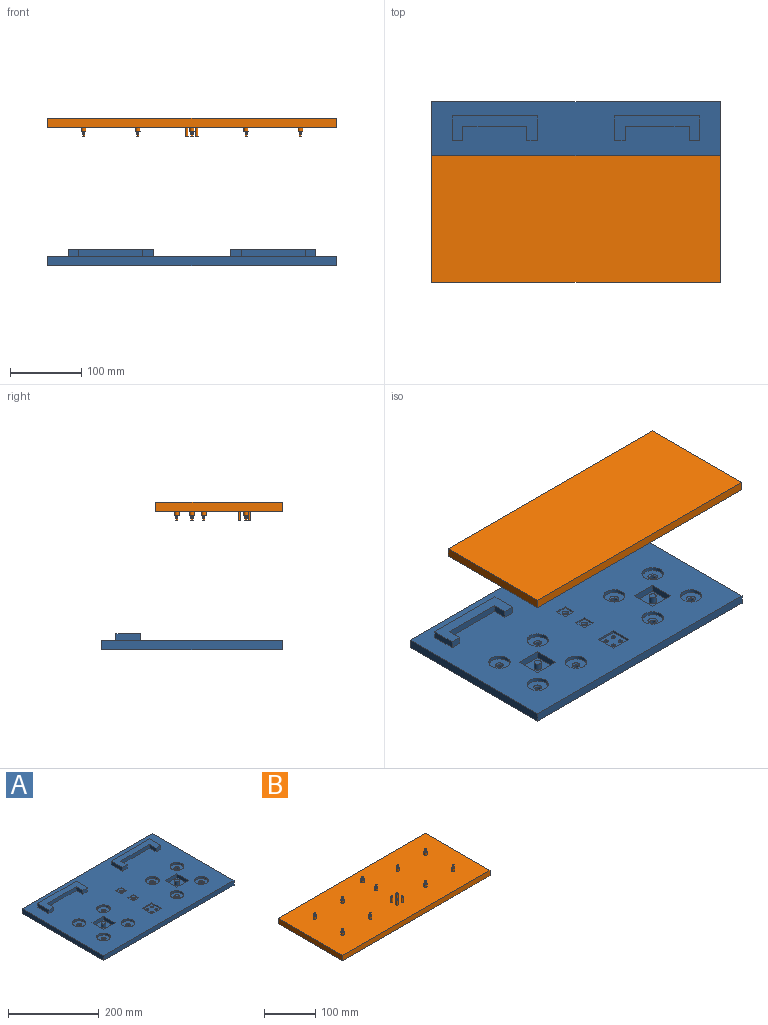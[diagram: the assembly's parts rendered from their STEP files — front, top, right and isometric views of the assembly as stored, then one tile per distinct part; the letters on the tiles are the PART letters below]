
ASSEMBLY  parts=2 mates=2
PART A: 93 faces, bbox 406.4x254x22.7 mm
  f0: plane 406.4x254mm, normal (0,0,1), area 88690.8mm2, adj f2,f3,f4,f5,f6,f7,f8,f9
  f1: plane 406.4x254mm, normal (0,0,-1), area 102653.3mm2, adj f2,f3,f4,f5,f21,f22,f23,f24
  f2: plane 406.4x12.7mm, normal (0,1,0), area 5161.3mm2, adj f0,f1,f3,f5
  f3: plane 254x12.7mm, normal (-1,0,0), area 3225.8mm2, adj f0,f1,f2,f4
  f4: plane 406.4x12.7mm, normal (0,-1,0), area 5161.3mm2, adj f0,f1,f3,f5
  f5: plane 254x12.7mm, normal (1,0,0), area 3225.8mm2, adj f0,f1,f2,f4
  f6: plane 17.15x2mm, normal (0,-1,0), area 34.3mm2, adj f0,f7,f9,f10
  f7: plane 17.15x2mm, normal (1,0,0), area 34.3mm2, adj f0,f6,f8,f10
  f8: plane 17.15x2mm, normal (0,1,0), area 34.3mm2, adj f0,f7,f9,f10
  f9: plane 17.15x2mm, normal (-1,0,0), area 34.3mm2, adj f0,f6,f8,f10
  f10: plane 17.15x17.15mm, normal (0,0,1), area 226.3mm2, adj f6,f7,f8,f9,f83
  f11: plane 17.15x2mm, normal (-1,0,0), area 34.3mm2, adj f0,f12,f14,f15
  f12: plane 17.15x2mm, normal (0,-1,0), area 34.3mm2, adj f0,f11,f13,f15
  f13: plane 17.15x2mm, normal (1,0,0), area 34.3mm2, adj f0,f12,f14,f15
  f14: plane 17.15x2mm, normal (0,1,0), area 34.3mm2, adj f0,f11,f13,f15
  f15: plane 17.15x17.15mm, normal (0,0,1), area 226.3mm2, adj f11,f12,f13,f14,f84
  f16: plane 30x3mm, normal (0,-1,0), area 90mm2, adj f0,f17,f19,f20
  f17: plane 30x3mm, normal (1,0,0), area 90mm2, adj f0,f16,f18,f20
  f18: plane 30x3mm, normal (0,1,0), area 90mm2, adj f0,f17,f19,f20
  f19: plane 30x3mm, normal (-1,0,0), area 90mm2, adj f0,f16,f18,f20
  f20: plane 30x30mm, normal (0,0,1), area 786.9mm2, adj f16,f17,f18,f19,f21,f22,f23,f24
  f21: cylinder r=3mm len=9.7mm, axis (0,0,1), area 182.8mm2, adj f1,f20
  f22: cylinder r=3mm len=9.7mm, axis (0,0,1), area 182.8mm2, adj f1,f20
  f23: cylinder r=3mm len=9.7mm, axis (0,0,1), area 182.8mm2, adj f1,f20
  f24: cylinder r=3mm len=9.7mm, axis (0,0,1), area 182.8mm2, adj f1,f20
  f25: cylinder r=15mm len=30mm, axis (0,0,1), area 471.2mm2, adj f0,f26
  f26: plane 30x30mm, normal (0,0,1), area 614.1mm2, adj f25,f92
  f27: cylinder r=15mm len=30mm, axis (0,0,1), area 471.2mm2, adj f0,f28
  f28: plane 30x30mm, normal (0,0,1), area 573.8mm2, adj f27,f85
  f29: cylinder r=15mm len=30mm, axis (0,0,1), area 471.2mm2, adj f0,f30
  f30: plane 30x30mm, normal (0,0,1), area 573.8mm2, adj f29,f86
  f31: cylinder r=15mm len=30mm, axis (0,0,1), area 471.2mm2, adj f0,f32
  f32: plane 30x30mm, normal (0,0,1), area 573.8mm2, adj f31,f87
  f33: cylinder r=15mm len=30mm, axis (0,0,1), area 471.2mm2, adj f0,f34
  f34: plane 30x30mm, normal (0,0,1), area 614.1mm2, adj f33,f89
  f35: cylinder r=15mm len=30mm, axis (0,0,1), area 471.2mm2, adj f0,f36
  f36: plane 30x30mm, normal (0,0,1), area 614.1mm2, adj f35,f90
  f37: cylinder r=15mm len=30mm, axis (0,0,1), area 471.2mm2, adj f0,f38
  f38: plane 30x30mm, normal (0,0,1), area 614.1mm2, adj f37,f91
  f39: cylinder r=15mm len=30mm, axis (0,0,1), area 471.2mm2, adj f0,f40
  f40: plane 30x30mm, normal (0,0,1), area 573.8mm2, adj f39,f88
  f41: cylinder r=3.97mm len=7.94mm, axis (0,0,1), area 128.7mm2, adj f1,f92
  f42: cylinder r=3.97mm len=7.94mm, axis (0,0,1), area 155.4mm2, adj f1,f85
  f43: cylinder r=3.97mm len=7.94mm, axis (0,0,1), area 155.4mm2, adj f1,f86
  f44: cylinder r=3.97mm len=7.94mm, axis (0,0,1), area 155.4mm2, adj f1,f87
  f45: cylinder r=3.97mm len=7.94mm, axis (0,0,1), area 128.7mm2, adj f1,f89
  f46: cylinder r=3.97mm len=7.94mm, axis (0,0,1), area 128.7mm2, adj f1,f90
  f47: cylinder r=3.97mm len=7.94mm, axis (0,0,1), area 128.7mm2, adj f1,f91
  f48: cylinder r=3.97mm len=7.94mm, axis (0,0,1), area 155.4mm2, adj f1,f88
  f49: plane 36x10mm, normal (-1,0,0), area 360mm2, adj f0,f50,f52,f53
  f50: plane 36x10mm, normal (0,-1,0), area 360mm2, adj f0,f49,f51,f53
  f51: plane 36x10mm, normal (1,0,0), area 360mm2, adj f0,f50,f52,f53
  f52: plane 36x10mm, normal (0,1,0), area 360mm2, adj f0,f49,f51,f53
  f53: plane 36x36mm, normal (0,0,1), area 1217.5mm2, adj f49,f50,f51,f52,f61
  f54: plane 36x10mm, normal (0,-1,0), area 360mm2, adj f0,f55,f57,f58
  f55: plane 36x10mm, normal (1,0,0), area 360mm2, adj f0,f54,f56,f58
  f56: plane 36x10mm, normal (0,1,0), area 360mm2, adj f0,f55,f57,f58
  f57: plane 36x10mm, normal (-1,0,0), area 360mm2, adj f0,f54,f56,f58
  f58: plane 36x36mm, normal (0,0,1), area 1217.5mm2, adj f54,f55,f56,f57,f59
  f59: cylinder r=5mm len=10mm, axis (0,0,-1), area 314.2mm2, adj f58,f60
  f60: plane 10x10mm, normal (0,0,1), area 78.5mm2, adj f59
  f61: cylinder r=5mm len=10mm, axis (0,0,-1), area 314.2mm2, adj f53,f62
  f62: plane 10x10mm, normal (0,0,1), area 78.5mm2, adj f61
  f63: plane 35x10mm, normal (-1,0,0), area 350mm2, adj f0,f64,f70,f71
  f64: plane 15x10mm, normal (0,-1,0), area 150mm2, adj f0,f63,f65,f71
  f65: plane 20x10mm, normal (1,0,0), area 200mm2, adj f0,f64,f66,f71
  f66: plane 90x10mm, normal (0,-1,0), area 900mm2, adj f0,f65,f67,f71
  f67: plane 20x10mm, normal (-1,0,0), area 200mm2, adj f0,f66,f68,f71
  f68: plane 15x10mm, normal (0,-1,0), area 150mm2, adj f0,f67,f69,f71
  f69: plane 35x10mm, normal (1,0,0), area 350mm2, adj f0,f68,f70,f71
  f70: plane 120x10mm, normal (0,1,0), area 1200mm2, adj f0,f63,f69,f71
  f71: plane 120x35mm, normal (0,0,1), area 2400mm2, adj f63,f64,f65,f66,f67,f68,f69,f70
  f72: plane 20x10mm, normal (-1,0,0), area 200mm2, adj f0,f73,f79,f80
  f73: plane 15x10mm, normal (0,-1,0), area 150mm2, adj f0,f72,f74,f80
  f74: plane 35x10mm, normal (1,0,0), area 350mm2, adj f0,f73,f75,f80
  f75: plane 120x10mm, normal (0,1,0), area 1200mm2, adj f0,f74,f76,f80
  f76: plane 35x10mm, normal (-1,0,0), area 350mm2, adj f0,f75,f77,f80
  f77: plane 15x10mm, normal (0,-1,0), area 150mm2, adj f0,f76,f78,f80
  f78: plane 20x10mm, normal (1,0,0), area 200mm2, adj f0,f77,f79,f80
  f79: plane 90x10mm, normal (0,-1,0), area 900mm2, adj f0,f72,f78,f80
  f80: plane 120x35mm, normal (0,0,1), area 2400mm2, adj f72,f73,f74,f75,f76,f77,f78,f79
  f81: cylinder r=3.17mm len=8.16mm, axis (0,0,1), area 162.8mm2, adj f1,f83
  f82: cylinder r=3.17mm len=8.16mm, axis (0,0,1), area 162.8mm2, adj f1,f84
  f83: cone r=3.17mm half-angle=30deg, axis (0,0,1), area 72mm2, adj f10,f81
  f84: cone r=3.17mm half-angle=30deg, axis (0,0,1), area 72mm2, adj f15,f82
  f85: cone r=6.51mm half-angle=60deg, axis (0,0,1), area 96.5mm2, adj f28,f42
  f86: cone r=6.51mm half-angle=60deg, axis (0,0,1), area 96.5mm2, adj f30,f43
  f87: cone r=6.51mm half-angle=60deg, axis (0,0,1), area 96.5mm2, adj f32,f44
  f88: cone r=6.51mm half-angle=60deg, axis (0,0,1), area 96.5mm2, adj f40,f48
  f89: cone r=3.97mm half-angle=30deg, axis (0,0,1), area 86.6mm2, adj f34,f45
  f90: cone r=3.97mm half-angle=30deg, axis (0,0,1), area 86.6mm2, adj f36,f46
  f91: cone r=3.97mm half-angle=30deg, axis (0,0,1), area 86.6mm2, adj f38,f47
  f92: cone r=3.97mm half-angle=30deg, axis (0,0,1), area 86.6mm2, adj f26,f41
PART B: 152 faces, bbox 406.4x177.8x25.4 mm
  f0: plane 406.4x177.8mm, normal (0,0,1), area 71891mm2, adj f1,f2,f3,f4,f6,f21,f36,f51
  f1: plane 406.4x12.7mm, normal (0,1,0), area 5161.3mm2, adj f0,f2,f4,f5
  f2: plane 177.8x12.7mm, normal (-1,0,0), area 2258.1mm2, adj f0,f1,f3,f5
  f3: plane 406.4x12.7mm, normal (0,-1,0), area 5161.3mm2, adj f0,f2,f4,f5
  f4: plane 177.8x12.7mm, normal (1,0,0), area 2258.1mm2, adj f0,f1,f3,f5
  f5: plane 406.4x177.8mm, normal (0,0,-1), area 72257.9mm2, adj f1,f2,f3,f4
  f6: cylinder r=3.17mm len=6.35mm, axis (0,0,-1), area 126.7mm2, adj f0,f7
  f7: plane 6.35x6.35mm, normal (0,0,1), area 25.8mm2, adj f6,f9,f10,f11,f12,f13,f14,f15
  f8: plane 3.67x3.18mm, normal (0,0,1), area 5.8mm2, adj f9,f10,f11,f12,f13,f14,f15,f16
  f9: plane 6.35x0.92mm, normal (-0.87,-0.5,0), area 6.7mm2, adj f7,f8,f10,f20
  f10: plane 6.35x1.06mm, normal (0,-1,0), area 6.7mm2, adj f7,f8,f9,f11
  f11: plane 6.35x0.92mm, normal (-0.87,0.5,0), area 6.7mm2, adj f7,f8,f10,f12
  f12: plane 6.35x0.92mm, normal (-0.87,-0.5,0), area 6.7mm2, adj f7,f8,f11,f13
  f13: plane 6.35x1.06mm, normal (0,1,0), area 6.7mm2, adj f7,f8,f12,f14
  f14: plane 6.35x0.92mm, normal (-0.87,0.5,0), area 6.7mm2, adj f7,f8,f13,f15
  f15: plane 6.35x0.92mm, normal (0.87,0.5,0), area 6.7mm2, adj f7,f8,f14,f16
  f16: plane 6.35x1.06mm, normal (0,1,0), area 6.7mm2, adj f7,f8,f15,f17
  f17: plane 6.35x0.92mm, normal (0.87,-0.5,0), area 6.7mm2, adj f7,f8,f16,f18
  f18: plane 6.35x0.92mm, normal (0.87,0.5,0), area 6.7mm2, adj f7,f8,f17,f19
  f19: plane 6.35x1.06mm, normal (0,-1,0), area 6.7mm2, adj f7,f8,f18,f20
  f20: plane 6.35x0.92mm, normal (0.87,-0.5,0), area 6.7mm2, adj f7,f8,f9,f19
  f21: cylinder r=3.17mm len=6.35mm, axis (0,0,-1), area 126.7mm2, adj f0,f22
  f22: plane 6.35x6.35mm, normal (0,0,1), area 25.8mm2, adj f21,f24,f25,f26,f27,f28,f29,f30
  f23: plane 3.67x3.18mm, normal (0,0,1), area 5.8mm2, adj f24,f25,f26,f27,f28,f29,f30,f31
  f24: plane 6.35x0.92mm, normal (0.87,-0.5,0), area 6.7mm2, adj f22,f23,f25,f35
  f25: plane 6.35x0.92mm, normal (-0.87,-0.5,0), area 6.7mm2, adj f22,f23,f24,f26
  f26: plane 6.35x1.06mm, normal (0,-1,0), area 6.7mm2, adj f22,f23,f25,f27
  f27: plane 6.35x0.92mm, normal (-0.87,0.5,0), area 6.7mm2, adj f22,f23,f26,f28
  f28: plane 6.35x0.92mm, normal (-0.87,-0.5,0), area 6.7mm2, adj f22,f23,f27,f29
  f29: plane 6.35x1.06mm, normal (0,1,0), area 6.7mm2, adj f22,f23,f28,f30
  f30: plane 6.35x0.92mm, normal (-0.87,0.5,0), area 6.7mm2, adj f22,f23,f29,f31
  f31: plane 6.35x0.92mm, normal (0.87,0.5,0), area 6.7mm2, adj f22,f23,f30,f32
  f32: plane 6.35x1.06mm, normal (0,1,0), area 6.7mm2, adj f22,f23,f31,f33
  f33: plane 6.35x0.92mm, normal (0.87,-0.5,0), area 6.7mm2, adj f22,f23,f32,f34
  f34: plane 6.35x0.92mm, normal (0.87,0.5,0), area 6.7mm2, adj f22,f23,f33,f35
  f35: plane 6.35x1.06mm, normal (0,-1,0), area 6.7mm2, adj f22,f23,f24,f34
  f36: cylinder r=3.17mm len=6.35mm, axis (0,0,-1), area 126.7mm2, adj f0,f37
  f37: plane 6.35x6.35mm, normal (0,0,1), area 25.8mm2, adj f36,f39,f40,f41,f42,f43,f44,f45
  f38: plane 3.67x3.18mm, normal (0,0,1), area 5.8mm2, adj f39,f40,f41,f42,f43,f44,f45,f46
  f39: plane 6.35x0.92mm, normal (0.87,-0.5,0), area 6.7mm2, adj f37,f38,f40,f50
  f40: plane 6.35x0.92mm, normal (-0.87,-0.5,0), area 6.7mm2, adj f37,f38,f39,f41
  f41: plane 6.35x1.06mm, normal (0,-1,0), area 6.7mm2, adj f37,f38,f40,f42
  f42: plane 6.35x0.92mm, normal (-0.87,0.5,0), area 6.7mm2, adj f37,f38,f41,f43
  f43: plane 6.35x0.92mm, normal (-0.87,-0.5,0), area 6.7mm2, adj f37,f38,f42,f44
  f44: plane 6.35x1.06mm, normal (0,1,0), area 6.7mm2, adj f37,f38,f43,f45
  f45: plane 6.35x0.92mm, normal (-0.87,0.5,0), area 6.7mm2, adj f37,f38,f44,f46
  f46: plane 6.35x0.92mm, normal (0.87,0.5,0), area 6.7mm2, adj f37,f38,f45,f47
  f47: plane 6.35x1.06mm, normal (0,1,0), area 6.7mm2, adj f37,f38,f46,f48
  f48: plane 6.35x0.92mm, normal (0.87,-0.5,0), area 6.7mm2, adj f37,f38,f47,f49
  f49: plane 6.35x0.92mm, normal (0.87,0.5,0), area 6.7mm2, adj f37,f38,f48,f50
  f50: plane 6.35x1.06mm, normal (0,-1,0), area 6.7mm2, adj f37,f38,f39,f49
  f51: cylinder r=3.17mm len=6.35mm, axis (0,0,-1), area 126.7mm2, adj f0,f52
  f52: plane 6.35x6.35mm, normal (0,0,1), area 25.8mm2, adj f51,f54,f55,f56,f57,f58,f59,f60
  f53: plane 3.67x3.18mm, normal (0,0,1), area 5.8mm2, adj f54,f55,f56,f57,f58,f59,f60,f61
  f54: plane 6.35x0.92mm, normal (-0.87,-0.5,0), area 6.7mm2, adj f52,f53,f55,f65
  f55: plane 6.35x1.06mm, normal (0,-1,0), area 6.7mm2, adj f52,f53,f54,f56
  f56: plane 6.35x0.92mm, normal (-0.87,0.5,0), area 6.7mm2, adj f52,f53,f55,f57
  f57: plane 6.35x0.92mm, normal (-0.87,-0.5,0), area 6.7mm2, adj f52,f53,f56,f58
  f58: plane 6.35x1.06mm, normal (0,1,0), area 6.7mm2, adj f52,f53,f57,f59
  f59: plane 6.35x0.92mm, normal (-0.87,0.5,0), area 6.7mm2, adj f52,f53,f58,f60
  f60: plane 6.35x0.92mm, normal (0.87,0.5,0), area 6.7mm2, adj f52,f53,f59,f61
  f61: plane 6.35x1.06mm, normal (0,1,0), area 6.7mm2, adj f52,f53,f60,f62
  f62: plane 6.35x0.92mm, normal (0.87,-0.5,0), area 6.7mm2, adj f52,f53,f61,f63
  f63: plane 6.35x0.92mm, normal (0.87,0.5,0), area 6.7mm2, adj f52,f53,f62,f64
  f64: plane 6.35x1.06mm, normal (0,-1,0), area 6.7mm2, adj f52,f53,f63,f65
  f65: plane 6.35x0.92mm, normal (0.87,-0.5,0), area 6.7mm2, adj f52,f53,f54,f64
  f66: cylinder r=3.17mm len=6.35mm, axis (0,0,-1), area 126.7mm2, adj f0,f67
  f67: plane 6.35x6.35mm, normal (0,0,1), area 25.8mm2, adj f66,f69,f70,f71,f72,f73,f74,f75
  f68: plane 3.67x3.18mm, normal (0,0,1), area 5.8mm2, adj f69,f70,f71,f72,f73,f74,f75,f76
  f69: plane 6.35x1.06mm, normal (0,1,0), area 6.7mm2, adj f67,f68,f70,f80
  f70: plane 6.35x0.92mm, normal (0.87,-0.5,0), area 6.7mm2, adj f67,f68,f69,f71
  f71: plane 6.35x0.92mm, normal (0.87,0.5,0), area 6.7mm2, adj f67,f68,f70,f72
  f72: plane 6.35x1.06mm, normal (0,-1,0), area 6.7mm2, adj f67,f68,f71,f73
  f73: plane 6.35x0.92mm, normal (0.87,-0.5,0), area 6.7mm2, adj f67,f68,f72,f74
  f74: plane 6.35x0.92mm, normal (-0.87,-0.5,0), area 6.7mm2, adj f67,f68,f73,f75
  f75: plane 6.35x1.06mm, normal (0,-1,0), area 6.7mm2, adj f67,f68,f74,f76
  f76: plane 6.35x0.92mm, normal (-0.87,0.5,0), area 6.7mm2, adj f67,f68,f75,f77
  f77: plane 6.35x0.92mm, normal (-0.87,-0.5,0), area 6.7mm2, adj f67,f68,f76,f78
  f78: plane 6.35x1.06mm, normal (0,1,0), area 6.7mm2, adj f67,f68,f77,f79
  f79: plane 6.35x0.92mm, normal (-0.87,0.5,0), area 6.7mm2, adj f67,f68,f78,f80
  f80: plane 6.35x0.92mm, normal (0.87,0.5,0), area 6.7mm2, adj f67,f68,f69,f79
  f81: cylinder r=3.17mm len=6.35mm, axis (0,0,-1), area 126.7mm2, adj f0,f82
  f82: plane 6.35x6.35mm, normal (0,0,1), area 25.8mm2, adj f81,f84,f85,f86,f87,f88,f89,f90
  f83: plane 3.67x3.18mm, normal (0,0,1), area 5.8mm2, adj f84,f85,f86,f87,f88,f89,f90,f91
  f84: plane 6.35x0.92mm, normal (-0.87,0.5,0), area 6.7mm2, adj f82,f83,f85,f95
  f85: plane 6.35x0.92mm, normal (0.87,0.5,0), area 6.7mm2, adj f82,f83,f84,f86
  f86: plane 6.35x1.06mm, normal (0,1,0), area 6.7mm2, adj f82,f83,f85,f87
  f87: plane 6.35x0.92mm, normal (0.87,-0.5,0), area 6.7mm2, adj f82,f83,f86,f88
  f88: plane 6.35x0.92mm, normal (0.87,0.5,0), area 6.7mm2, adj f82,f83,f87,f89
  f89: plane 6.35x1.06mm, normal (0,-1,0), area 6.7mm2, adj f82,f83,f88,f90
  f90: plane 6.35x0.92mm, normal (0.87,-0.5,0), area 6.7mm2, adj f82,f83,f89,f91
  f91: plane 6.35x0.92mm, normal (-0.87,-0.5,0), area 6.7mm2, adj f82,f83,f90,f92
  f92: plane 6.35x1.06mm, normal (0,-1,0), area 6.7mm2, adj f82,f83,f91,f93
  f93: plane 6.35x0.92mm, normal (-0.87,0.5,0), area 6.7mm2, adj f82,f83,f92,f94
  f94: plane 6.35x0.92mm, normal (-0.87,-0.5,0), area 6.7mm2, adj f82,f83,f93,f95
  f95: plane 6.35x1.06mm, normal (0,1,0), area 6.7mm2, adj f82,f83,f84,f94
  f96: cylinder r=3.17mm len=6.35mm, axis (0,0,-1), area 126.7mm2, adj f0,f97
  f97: plane 6.35x6.35mm, normal (0,0,1), area 25.8mm2, adj f96,f99,f100,f101,f102,f103,f104,f105
  f98: plane 3.67x3.18mm, normal (0,0,1), area 5.8mm2, adj f99,f100,f101,f102,f103,f104,f105,f106
  f99: plane 6.35x0.92mm, normal (0.87,0.5,0), area 6.7mm2, adj f97,f98,f100,f110
  f100: plane 6.35x1.06mm, normal (0,1,0), area 6.7mm2, adj f97,f98,f99,f101
  f101: plane 6.35x0.92mm, normal (0.87,-0.5,0), area 6.7mm2, adj f97,f98,f100,f102
  f102: plane 6.35x0.92mm, normal (0.87,0.5,0), area 6.7mm2, adj f97,f98,f101,f103
  f103: plane 6.35x1.06mm, normal (0,-1,0), area 6.7mm2, adj f97,f98,f102,f104
  f104: plane 6.35x0.92mm, normal (0.87,-0.5,0), area 6.7mm2, adj f97,f98,f103,f105
  f105: plane 6.35x0.92mm, normal (-0.87,-0.5,0), area 6.7mm2, adj f97,f98,f104,f106
  f106: plane 6.35x1.06mm, normal (0,-1,0), area 6.7mm2, adj f97,f98,f105,f107
  f107: plane 6.35x0.92mm, normal (-0.87,0.5,0), area 6.7mm2, adj f97,f98,f106,f108
  f108: plane 6.35x0.92mm, normal (-0.87,-0.5,0), area 6.7mm2, adj f97,f98,f107,f109
  f109: plane 6.35x1.06mm, normal (0,1,0), area 6.7mm2, adj f97,f98,f108,f110
  f110: plane 6.35x0.92mm, normal (-0.87,0.5,0), area 6.7mm2, adj f97,f98,f99,f109
  f111: cylinder r=3.17mm len=6.35mm, axis (0,0,-1), area 126.7mm2, adj f0,f112
  f112: plane 6.35x6.35mm, normal (0,0,1), area 25.8mm2, adj f111,f114,f115,f116,f117,f118,f119,f120
  f113: plane 3.67x3.18mm, normal (0,0,1), area 5.8mm2, adj f114,f115,f116,f117,f118,f119,f120,f121
  f114: plane 6.35x0.92mm, normal (0.87,0.5,0), area 6.7mm2, adj f112,f113,f115,f125
  f115: plane 6.35x1.06mm, normal (0,-1,0), area 6.7mm2, adj f112,f113,f114,f116
  f116: plane 6.35x0.92mm, normal (0.87,-0.5,0), area 6.7mm2, adj f112,f113,f115,f117
  f117: plane 6.35x0.92mm, normal (-0.87,-0.5,0), area 6.7mm2, adj f112,f113,f116,f118
  f118: plane 6.35x1.06mm, normal (0,-1,0), area 6.7mm2, adj f112,f113,f117,f119
  f119: plane 6.35x0.92mm, normal (-0.87,0.5,0), area 6.7mm2, adj f112,f113,f118,f120
  f120: plane 6.35x0.92mm, normal (-0.87,-0.5,0), area 6.7mm2, adj f112,f113,f119,f121
  f121: plane 6.35x1.06mm, normal (0,1,0), area 6.7mm2, adj f112,f113,f120,f122
  f122: plane 6.35x0.92mm, normal (-0.87,0.5,0), area 6.7mm2, adj f112,f113,f121,f123
  f123: plane 6.35x0.92mm, normal (0.87,0.5,0), area 6.7mm2, adj f112,f113,f122,f124
  f124: plane 6.35x1.06mm, normal (0,1,0), area 6.7mm2, adj f112,f113,f123,f125
  f125: plane 6.35x0.92mm, normal (0.87,-0.5,0), area 6.7mm2, adj f112,f113,f114,f124
  f126: cylinder r=2mm len=12.7mm, axis (0,0,-1), area 159.6mm2, adj f0,f127
  f127: plane 4x4mm, normal (0,0,1), area 12.6mm2, adj f126
  f128: cylinder r=2mm len=12.7mm, axis (0,0,-1), area 159.6mm2, adj f0,f129
  f129: plane 4x4mm, normal (0,0,1), area 12.6mm2, adj f128
  f130: cylinder r=2mm len=12.7mm, axis (0,0,-1), area 159.6mm2, adj f0,f131
  f131: plane 4x4mm, normal (0,0,1), area 12.6mm2, adj f130
  f132: cylinder r=2mm len=12.7mm, axis (0,0,-1), area 159.6mm2, adj f0,f133
  f133: plane 4x4mm, normal (0,0,1), area 12.6mm2, adj f132
  f134: cylinder r=3.17mm len=6.35mm, axis (0,0,-1), area 126.7mm2, adj f0,f135
  f135: plane 6.35x6.35mm, normal (0,0,1), area 25.1mm2, adj f134,f137,f138,f139,f140,f141,f142
  f136: plane 3.18x2.75mm, normal (0,0,1), area 6.5mm2, adj f137,f138,f139,f140,f141,f142
  f137: plane 6.35x1.38mm, normal (0.87,0.5,0), area 10.1mm2, adj f135,f136,f138,f142
  f138: plane 6.35x1.38mm, normal (0.87,-0.5,0), area 10.1mm2, adj f135,f136,f137,f139
  f139: plane 6.35x1.59mm, normal (0,-1,0), area 10.1mm2, adj f135,f136,f138,f140
  f140: plane 6.35x1.38mm, normal (-0.87,-0.5,0), area 10.1mm2, adj f135,f136,f139,f141
  f141: plane 6.35x1.38mm, normal (-0.87,0.5,0), area 10.1mm2, adj f135,f136,f140,f142
  f142: plane 6.35x1.59mm, normal (0,1,0), area 10.1mm2, adj f135,f136,f137,f141
  f143: cylinder r=3.17mm len=6.35mm, axis (0,0,-1), area 126.7mm2, adj f0,f144
  f144: plane 6.35x6.35mm, normal (0,0,1), area 25.1mm2, adj f143,f146,f147,f148,f149,f150,f151
  f145: plane 3.18x2.75mm, normal (0,0,1), area 6.5mm2, adj f146,f147,f148,f149,f150,f151
  f146: plane 6.35x1.38mm, normal (0.87,0.5,0), area 10.1mm2, adj f144,f145,f147,f151
  f147: plane 6.35x1.38mm, normal (0.87,-0.5,0), area 10.1mm2, adj f144,f145,f146,f148
  f148: plane 6.35x1.59mm, normal (0,-1,0), area 10.1mm2, adj f144,f145,f147,f149
  f149: plane 6.35x1.38mm, normal (-0.87,-0.5,0), area 10.1mm2, adj f144,f145,f148,f150
  f150: plane 6.35x1.38mm, normal (-0.87,0.5,0), area 10.1mm2, adj f144,f145,f149,f151
  f151: plane 6.35x1.59mm, normal (0,1,0), area 10.1mm2, adj f144,f145,f146,f150
PLACE A t=(-85.83,-102.2,-90.32)mm fixed
PLACE B rot(axis=(0,1,0),180deg) t=(-85.83,-140.3,117.8)mm
MATE planar B.f3 <-> A.f4  axis (0,-1,0) through (-85.83,-229.2,111.45)mm
MATE planar B.f4 <-> A.f3  axis (-1,0,0) through (-289.03,-140.3,111.45)mm
